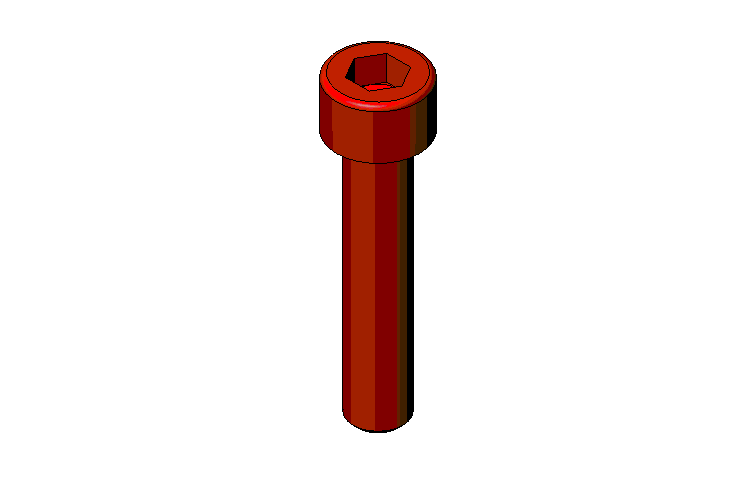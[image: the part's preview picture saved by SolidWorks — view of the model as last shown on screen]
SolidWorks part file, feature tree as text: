
SOLIDWORKS PART (.sldprt)
format: sldprt  version: not decoded by parser v0  size: 184,832 bytes
history: native  units: mm
features: plane x3, sketch x3, material x1, extrude x1, chamfer x1, revolve x1, cut_extrude x1 (+10 scaffold rows collapsed)
feature tree (21):
  scaffold x10  (default folders/planes/origin — collapsed)
  material  "Matériau <non spécifié>"
  plane  "Plan1"
  plane  "Plan2"
  plane  "Plan3"
  sketch  "Esquisse2"  dims[Diamètre nominal=6.0mm]
  extrude  "Base-Extrusion"  Depth=30mm Longueur sous tête=30mm
  chamfer  "Chanfrein1"  Distance=0.6mm Angle=45deg
  sketch  "Esquisse5"  dims[c1.D2=0.6mm c1.Hauteur tête=2.0mm c1.Cote sur plats=5.5mm c1.D3=~2.780036mm c2.D3=30.0deg c2.D4=2.75mm c2.Diamètre tête=10.0mm c2.Diamètre nominal=3.0mm c2.D1=5.0mm c3.D3=3.0mm c4.D3=60.0deg c4.Diamètre nominal=6.0mm c4.Cote sur plats=5.0mm c4.D4=3.0mm c4.D5=2.5mm]
  revolve  "Boss.-Révol.1"  Angle=360deg
  sketch  "Esquisse7"  dims[c1.D1=~2.410714mm c2.D1=30.0deg c2.D2=~1.370242mm c3.D2=30.0deg c3.D3=2.5mm]
  cut_extrude  "Enlèv. mat.-Extru.1"  Depth=3mm
decode coverage: 7 of 7 modeling features carry decoded parameters
note: ~ marks probable driven/reference dimensions
note: suppression state not decoded; provenance and decode notes live in map.json
